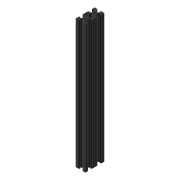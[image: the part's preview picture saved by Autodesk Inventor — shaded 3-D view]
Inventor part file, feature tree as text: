
AUTODESK INVENTOR PART (.ipt)
format: ipt  version: 2020 (Build 240168000, 168)  size: 131,072 bytes
history: native  units: mm
features: extrude x1
ambient origin geometry x8: Origin, YZ Plane, XZ Plane, XY Plane, X Axis, Y Axis, Z Axis, Center Point
bodies: Solid1 (feature_tree)
feature tree (1):
  extrude  "Extrusion2"  [1 undecoded]
note: 1 required parameter value undecoded (feature->parameter linkage not recoverable at this tier; creation-order binding heuristic only, values carry confidence <= 0.55)
